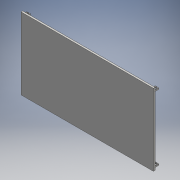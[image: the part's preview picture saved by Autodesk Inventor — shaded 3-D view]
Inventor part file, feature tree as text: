
AUTODESK INVENTOR PART (.ipt)
format: ipt  version: 2016 (Build 200138000, 138)  size: 129,024 bytes
history: native  units: mm
features: extrude x2, hole x2, sketch x2
ambient origin geometry x8: Origin, YZ Plane, XZ Plane, XY Plane, X Axis, Y Axis, Z Axis, Center Point
bodies: Solid1 (feature_tree)
feature tree (6):
  extrude  "Extrusion1"  Depth=65.0mm
  extrude  "Extrusion2"  Depth=59.5mm
  hole  "Hole1"  [1 undecoded]
  hole  "Hole2"  [1 undecoded]
  sketch  "Sketch1"  dims[d0=119.6mm d1=65.0mm]
  sketch  "Sketch2"  dims[d2=1.5mm d3=0.0mm d4=59.5mm d5=3.5mm d6=0.5mm d7=3.5mm d8=0.0mm d9=1.75mm d10=1.75mm d11=3.0mm d12=6.0mm d13=4.0mm d14=2.0mm d15=90.0deg d16=60.5mm d17=20.594885mm d18=1.75mm d19=1.75mm d20=3.0mm d21=6.0mm d22=4.0mm d23=2.0mm d24=90.0deg d25=60.5mm d26=20.594885mm]
note: 2 required parameter values undecoded (feature->parameter linkage not recoverable at this tier; creation-order binding heuristic only, values carry confidence <= 0.55)
